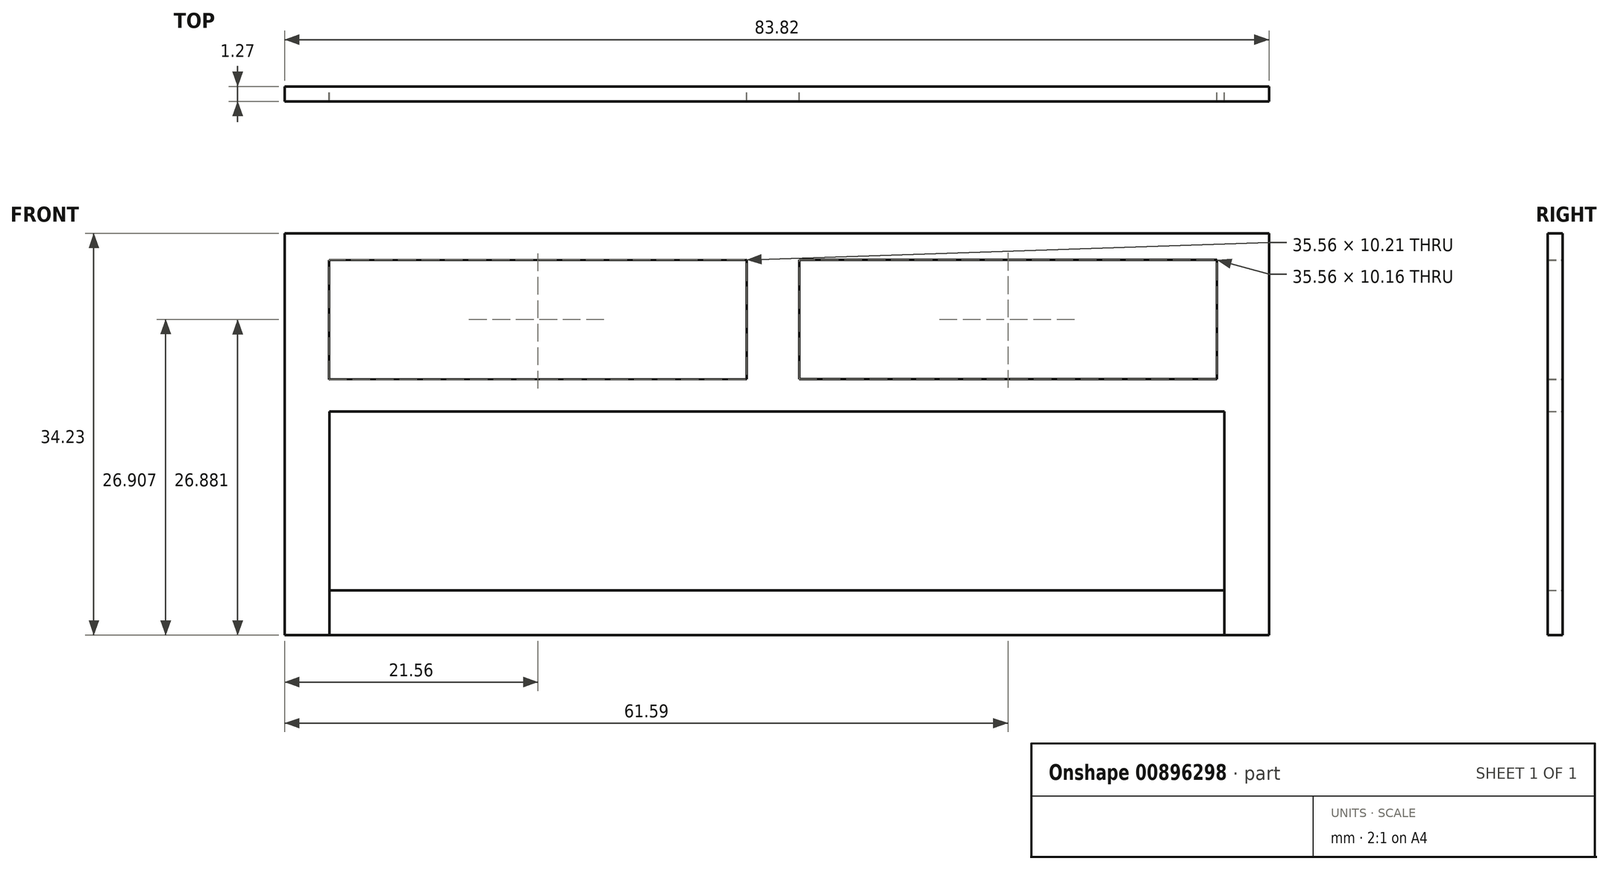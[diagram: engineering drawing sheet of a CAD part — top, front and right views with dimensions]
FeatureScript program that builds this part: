
annotation { "Feature Type Name" : "Feature", "Feature Type Description" : "" }
export const myFeature = defineFeature(function(context is Context, id is Id, definition is map)
    precondition{}
    {
        {
            var Q0;
            Q0=qCreatedBy(makeId("Front.planeOp"),FACE);
            var sketch = newSketch(context, id + "F0", { "sketchPlane" : qUnion([Q0])});
            skLineSegment(sketch, "E0.bottom", {"start": v(-38.1, -7.62) * mm, "end": v(38.1, -7.62) * mm});
            skLineSegment(sketch, "E0.top", {"start": v(-38.1, 7.62) * mm, "end": v(38.1, 7.62) * mm});
            skLineSegment(sketch, "E0.left", {"start": v(-38.1, -7.62) * mm, "end": v(-38.1, 7.62) * mm});
            skLineSegment(sketch, "E0.right", {"start": v(38.1, -7.62) * mm, "end": v(38.1, 7.62) * mm});
            skPoint(sketch, "E0.middle", {"position": v(0, 0) * mm});
            skLineSegment(sketch, "E1.bottom", {"start": v(-41.91, -11.43) * mm, "end": v(41.91, -11.43) * mm});
            skLineSegment(sketch, "E1.top", {"start": v(-41.91, 11.43) * mm, "end": v(41.91, 11.43) * mm});
            skLineSegment(sketch, "E1.left", {"start": v(-41.91, -11.43) * mm, "end": v(-41.91, 11.43) * mm});
            skLineSegment(sketch, "E1.right", {"start": v(41.91, -11.43) * mm, "end": v(41.91, 11.43) * mm});
            skLineSegment(sketch, "E2.top", {"start": v(-41.91, 18.73) * mm, "end": v(41.91, 18.73) * mm});
            skLineSegment(sketch, "E2.left", {"start": v(-41.91, 11.43) * mm, "end": v(-41.91, 18.73) * mm});
            skLineSegment(sketch, "E2.right", {"start": v(41.91, 11.43) * mm, "end": v(41.91, 18.73) * mm});
            skLineSegment(sketch, "E3", {"start": v(-38.1, 10.16) * mm, "end": v(38.1, 10.16) * mm});
            skLineSegment(sketch, "E4", {"start": v(-38.1, 10.16) * mm, "end": v(-38.1, 13.97) * mm});
            skLineSegment(sketch, "E5", {"start": v(38.1, 10.16) * mm, "end": v(38.1, 13.97) * mm});
            skLineSegment(sketch, "E6", {"start": v(-38.1, 13.97) * mm, "end": v(38.1, 13.97) * mm});
            skSolve(sketch);
        }
        {
            var Q0;
            Q0=makeQuery(id+"F0.imprint","IMPRINT",FACE,{"disambiguationData":[TD([[makeQuery(id+"F0.imprint","IMPRINT",EDGE,{"derivedFrom":sQuery(id+"F0.wireOp",EDGE,"E0.bottom")}),1.0]])]});
            extrude(context, id + "F1", {"entities" : qUnion([Q0]), "depth" : 1.27 * mm, "offsetDistance" : 25.4 * mm});
        }
        {
            var Q0;
            Q0=qCreatedBy(makeId("Front.planeOp"),FACE);
            var sketch = newSketch(context, id + "F2", { "sketchPlane" : qUnion([Q0])});
            skLineSegment(sketch, "E7.bottom", {"start": v(-38.1, -7.62) * mm, "end": v(38.1, -7.62) * mm});
            skLineSegment(sketch, "E7.top", {"start": v(-38.1, 7.62) * mm, "end": v(38.1, 7.62) * mm});
            skLineSegment(sketch, "E7.left", {"start": v(-38.1, -7.62) * mm, "end": v(-38.1, 7.62) * mm});
            skLineSegment(sketch, "E7.right", {"start": v(38.1, -7.62) * mm, "end": v(38.1, 7.62) * mm});
            skPoint(sketch, "E7.middle", {"position": v(0, 0) * mm});
            skLineSegment(sketch, "E8.top", {"start": v(-41.91, 11.43) * mm, "end": v(41.9, 11.43) * mm});
            skLineSegment(sketch, "E8.left", {"start": v(-41.91, -11.43) * mm, "end": v(-41.91, 11.43) * mm});
            skLineSegment(sketch, "E8.right", {"start": v(41.9, -11.43) * mm, "end": v(41.9, 11.43) * mm});
            skLineSegment(sketch, "E9.top", {"start": v(-41.91, 22.8) * mm, "end": v(41.9, 22.8) * mm});
            skLineSegment(sketch, "E9.left", {"start": v(-41.91, 11.43) * mm, "end": v(-41.91, 22.8) * mm});
            skLineSegment(sketch, "E9.right", {"start": v(41.9, 11.43) * mm, "end": v(41.9, 22.8) * mm});
            skLineSegment(sketch, "E10", {"start": v(-38.13, 10.35) * mm, "end": v(-2.57, 10.4) * mm});
            skLineSegment(sketch, "E11", {"start": v(-38.13, 10.35) * mm, "end": v(-38.13, 20.5) * mm});
            skLineSegment(sketch, "E12", {"start": v(-2.57, 10.4) * mm, "end": v(-2.57, 20.56) * mm});
            skLineSegment(sketch, "E13", {"start": v(-38.13, 20.5) * mm, "end": v(-2.57, 20.56) * mm});
            skLineSegment(sketch, "E14", {"start": v(-38.1, -7.62) * mm, "end": v(-38.1, -11.43) * mm});
            skLineSegment(sketch, "E15", {"start": v(-41.91, -11.43) * mm, "end": v(-38.1, -11.43) * mm});
            skLineSegment(sketch, "E16", {"start": v(38.1, -7.62) * mm, "end": v(38.1, -11.43) * mm});
            skLineSegment(sketch, "E17", {"start": v(38.1, -11.43) * mm, "end": v(41.9, -11.43) * mm});
            skLineSegment(sketch, "E18.bottom", {"start": v(1.9, 20.56) * mm, "end": v(37.46, 20.56) * mm});
            skLineSegment(sketch, "E18.top", {"start": v(1.9, 10.4) * mm, "end": v(37.46, 10.4) * mm});
            skLineSegment(sketch, "E18.left", {"start": v(1.9, 20.56) * mm, "end": v(1.9, 10.4) * mm});
            skLineSegment(sketch, "E18.right", {"start": v(37.46, 20.56) * mm, "end": v(37.46, 10.4) * mm});
            skSolve(sketch);
        }
        {
            var Q0;
            Q0=makeQuery(id+"F2.imprint","IMPRINT",FACE,{"disambiguationData":[TD([[makeQuery(id+"F2.imprint","IMPRINT",EDGE,{"derivedFrom":sQuery(id+"F2.wireOp",EDGE,"E9.top")}),-1.0]])]});
            var Q1;
            Q1=makeQuery(id+"F2.imprint","IMPRINT",FACE,{"disambiguationData":[TD([[makeQuery(id+"F2.imprint","IMPRINT",EDGE,{"derivedFrom":sQuery(id+"F2.wireOp",EDGE,"E7.bottom")}),-1.0]])]});
            var Q2;
            Q2=makeQuery(id+"F2.imprint","IMPRINT",FACE,{"disambiguationData":[TD([[makeQuery(id+"F2.imprint","IMPRINT",EDGE,{"derivedFrom":sQuery(id+"F2.wireOp",EDGE,"E7.top")}),1.0]])]});
            extrude(context, id + "F3", {"entities" : qUnion([Q0, Q1, Q2]), "depth" : 1.27 * mm, "offsetDistance" : 25.4 * mm});
        }
        {
            var Q0;
            Q0=qCreatedBy(makeId("Front.planeOp"),FACE);
            var sketch = newSketch(context, id + "F4", { "sketchPlane" : qUnion([Q0])});
            skLineSegment(sketch, "E19.bottom", {"start": v(-41.91, -11.43) * mm, "end": v(41.91, -11.43) * mm});
            skLineSegment(sketch, "E19.top", {"start": v(-41.91, 11.43) * mm, "end": v(41.91, 11.43) * mm});
            skLineSegment(sketch, "E19.left", {"start": v(-41.91, -11.43) * mm, "end": v(-41.91, 11.43) * mm});
            skLineSegment(sketch, "E19.right", {"start": v(41.91, -11.43) * mm, "end": v(41.91, 11.43) * mm});
            skPoint(sketch, "E19.middle", {"position": v(0, 0) * mm});
            skLineSegment(sketch, "E20", {"start": v(-41.91, -11.43) * mm, "end": v(-38.1, -11.43) * mm});
            skLineSegment(sketch, "E21", {"start": v(-38.1, -11.43) * mm, "end": v(-38.1, -7.62) * mm});
            skLineSegment(sketch, "E22", {"start": v(41.91, -11.43) * mm, "end": v(38.1, -11.43) * mm});
            skLineSegment(sketch, "E23", {"start": v(38.1, -11.43) * mm, "end": v(38.1, -7.62) * mm});
            skLineSegment(sketch, "E24", {"start": v(-38.1, -7.62) * mm, "end": v(38.1, -7.62) * mm});
            skLineSegment(sketch, "E25", {"start": v(38.1, -11.43) * mm, "end": v(-38.1, -11.43) * mm});
            skSolve(sketch);
        }
        {
            var Q0;
            {var subQ0=sQuery(id+"F4.wireOp",EDGE,"E21");Q0=makeQuery(id+"F4.imprint","IMPRINT",FACE,{"disambiguationData":[TD([[makeQuery(id+"F4.imprint","IMPRINT",EDGE,{"derivedFrom":subQ0}),-1.0]])]});}
            extrude(context, id + "F5", {"entities" : qUnion([Q0]), "depth" : 1.27 * mm, "offsetDistance" : 25.4 * mm});
        }
    });
